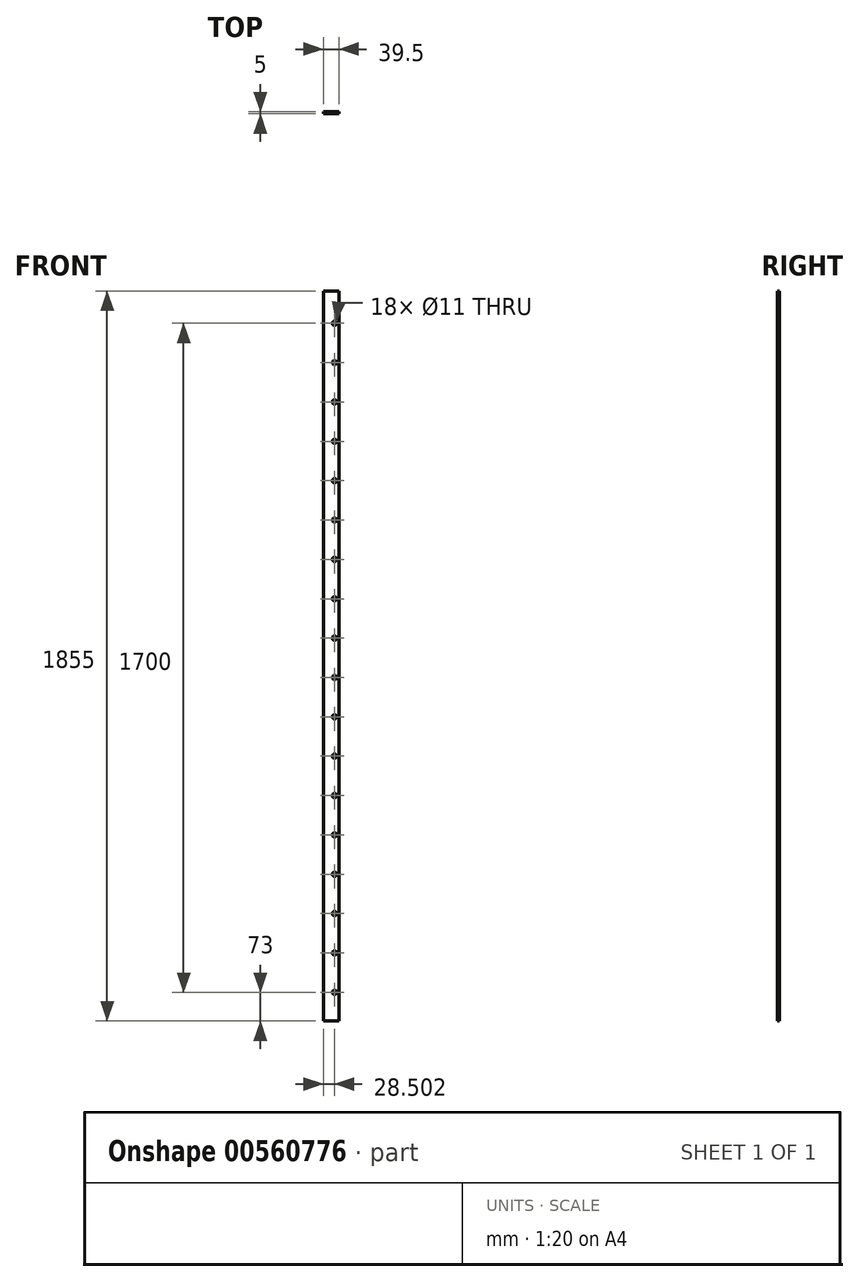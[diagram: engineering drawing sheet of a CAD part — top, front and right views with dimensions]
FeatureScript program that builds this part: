
annotation { "Feature Type Name" : "Feature", "Feature Type Description" : "" }
export const myFeature = defineFeature(function(context is Context, id is Id, definition is map)
    precondition{}
    {
        {
            var Q0;
            Q0=qCreatedBy(makeId("Front.planeOp"),FACE);
            var sketch = newSketch(context, id + "F0", { "sketchPlane" : qUnion([Q0])});
            skLineSegment(sketch, "E0", {"start": v(-203.74, -23.7) * mm, "end": v(-164.24, -23.7) * mm});
            skLineSegment(sketch, "E1", {"start": v(-164.24, -23.7) * mm, "end": v(-164.24, 1831.3) * mm});
            skLineSegment(sketch, "E2", {"start": v(-164.24, 1831.3) * mm, "end": v(-203.74, 1831.3) * mm});
            skLineSegment(sketch, "E3", {"start": v(-203.74, 1831.3) * mm, "end": v(-203.74, -23.7) * mm});
            skCircle(sketch, "E4", {"center": v(-175.24, 1749.3) * mm, "radius": 5.5 * mm});
            skPoint(sketch, "E4.centerSnap0", {"position": v(-175.24, 1780.9) * mm});
            skCircle(sketch, "E5.0.1.0", {"center": v(-175.24, 1649.3) * mm, "radius": 5.5 * mm});
            skCircle(sketch, "E5.0.2.0", {"center": v(-175.24, 1549.3) * mm, "radius": 5.5 * mm});
            skCircle(sketch, "E5.0.3.0", {"center": v(-175.24, 1449.3) * mm, "radius": 5.5 * mm});
            skCircle(sketch, "E5.0.4.0", {"center": v(-175.24, 1349.3) * mm, "radius": 5.5 * mm});
            skCircle(sketch, "E5.0.5.0", {"center": v(-175.24, 1249.3) * mm, "radius": 5.5 * mm});
            skCircle(sketch, "E5.0.6.0", {"center": v(-175.24, 1149.3) * mm, "radius": 5.5 * mm});
            skCircle(sketch, "E5.0.7.0", {"center": v(-175.24, 1049.3) * mm, "radius": 5.5 * mm});
            skCircle(sketch, "E5.0.8.0", {"center": v(-175.24, 949.3) * mm, "radius": 5.5 * mm});
            skCircle(sketch, "E5.0.9.0", {"center": v(-175.24, 849.3) * mm, "radius": 5.5 * mm});
            skCircle(sketch, "E5.0.10.0", {"center": v(-175.24, 749.3) * mm, "radius": 5.5 * mm});
            skCircle(sketch, "E5.0.11.0", {"center": v(-175.24, 649.3) * mm, "radius": 5.5 * mm});
            skCircle(sketch, "E5.0.12.0", {"center": v(-175.24, 549.3) * mm, "radius": 5.5 * mm});
            skCircle(sketch, "E5.0.13.0", {"center": v(-175.24, 449.3) * mm, "radius": 5.5 * mm});
            skCircle(sketch, "E5.0.14.0", {"center": v(-175.24, 349.3) * mm, "radius": 5.5 * mm});
            skCircle(sketch, "E5.0.15.0", {"center": v(-175.24, 249.3) * mm, "radius": 5.5 * mm});
            skCircle(sketch, "E5.0.16.0", {"center": v(-175.24, 149.3) * mm, "radius": 5.5 * mm});
            skCircle(sketch, "E5.0.17.0", {"center": v(-175.24, 49.3) * mm, "radius": 5.5 * mm});
            skLineSegment(sketch, "E5.direction1", {"start": v(-175.24, 1749.3) * mm, "end": v(-150.24, 1749.3) * mm, "construction": true});
            skLineSegment(sketch, "E5.direction2", {"start": v(-175.24, 1749.3) * mm, "end": v(-175.24, 1649.3) * mm, "construction": true});
            skSolve(sketch);
        }
        {
            var Q0;
            Q0 = qSketchRegion(id + "F0", true);
            var Q1;
            Q1=makeQuery(id+"F0.imprint","IMPRINT",FACE,{"disambiguationData":[TD([[makeQuery(id+"F0.imprint","IMPRINT",EDGE,{"derivedFrom":sQuery(id+"F0.wireOp",EDGE,"E0")}),1.0]])]});
            extrude(context, id + "F1", {"entities" : qUnion([Q0, Q1]), "depth" : 5 * mm, "offsetDistance" : 25 * mm});
        }
    });
